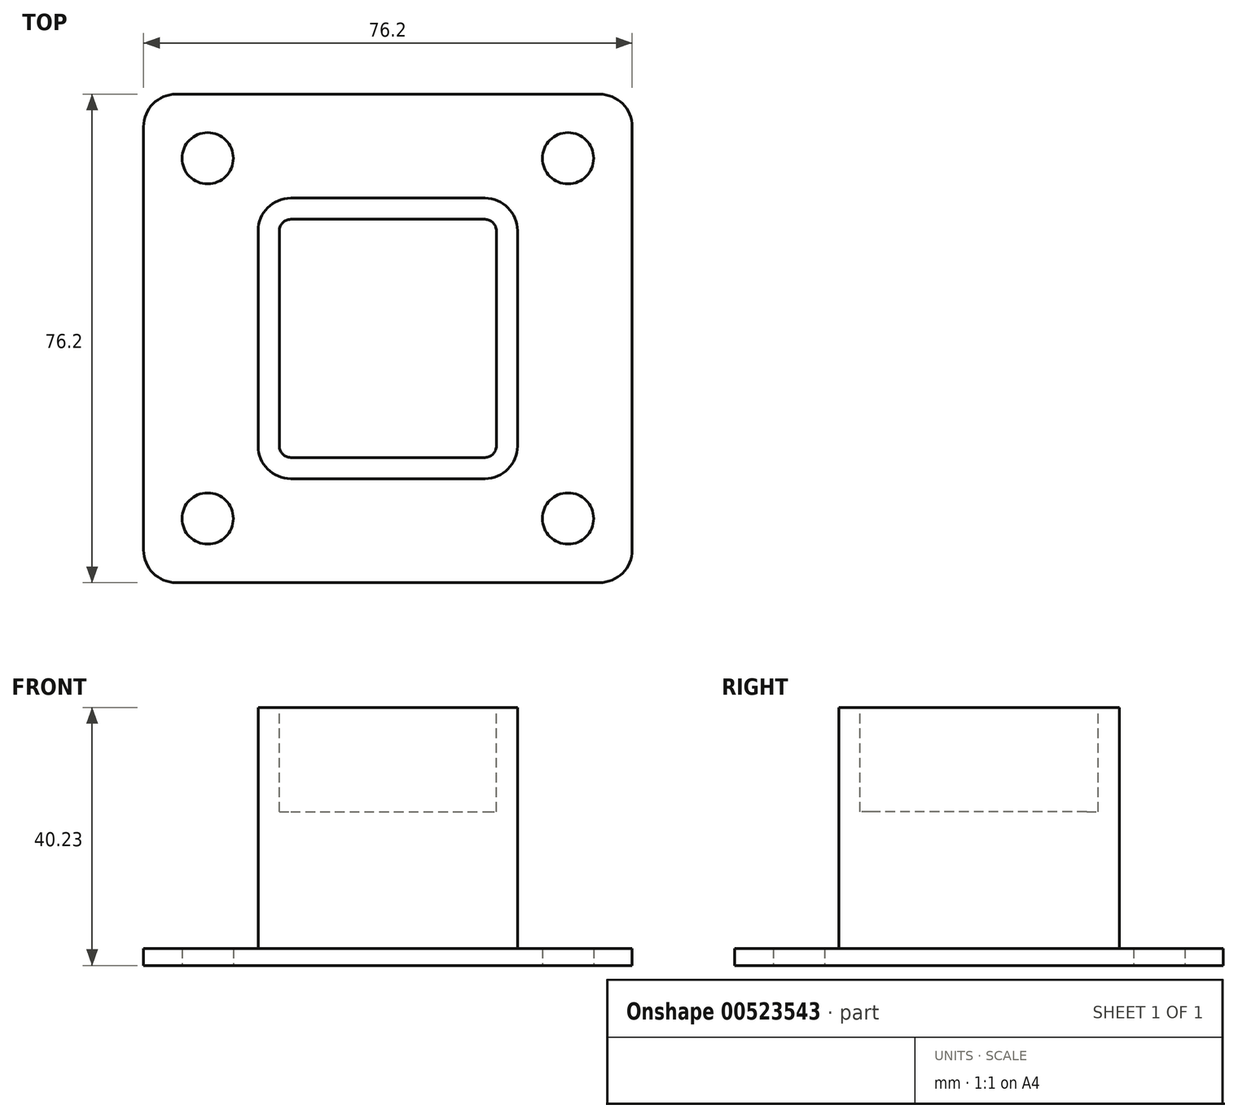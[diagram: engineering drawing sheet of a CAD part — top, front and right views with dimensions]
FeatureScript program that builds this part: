
annotation { "Feature Type Name" : "Feature", "Feature Type Description" : "" }
export const myFeature = defineFeature(function(context is Context, id is Id, definition is map)
    precondition{}
    {
        {
            var Q0;
            Q0=qCreatedBy(makeId("Top.planeOp"),FACE);
            var sketch = newSketch(context, id + "F0", { "sketchPlane" : qUnion([Q0])});
            skLineSegment(sketch, "E0.bottom", {"start": v(38.1, 38.1) * mm, "end": v(-38.1, 38.1) * mm});
            skLineSegment(sketch, "E0.top", {"start": v(38.1, -38.1) * mm, "end": v(-38.1, -38.1) * mm});
            skLineSegment(sketch, "E0.left", {"start": v(38.1, 38.1) * mm, "end": v(38.1, -38.1) * mm});
            skLineSegment(sketch, "E0.right", {"start": v(-38.1, 38.1) * mm, "end": v(-38.1, -38.1) * mm});
            skPoint(sketch, "E0.middle", {"position": v(0, 0) * mm});
            skLineSegment(sketch, "E1.bottom", {"start": v(28.1, 28.1) * mm, "end": v(-28.1, 28.1) * mm, "construction": true});
            skLineSegment(sketch, "E1.top", {"start": v(28.1, -28.1) * mm, "end": v(-28.1, -28.1) * mm, "construction": true});
            skLineSegment(sketch, "E1.left", {"start": v(28.1, 28.1) * mm, "end": v(28.1, -28.1) * mm, "construction": true});
            skLineSegment(sketch, "E1.right", {"start": v(-28.1, 28.1) * mm, "end": v(-28.1, -28.1) * mm, "construction": true});
            skCircle(sketch, "E2", {"center": v(-28.1, 28.1) * mm, "radius": 4 * mm});
            skCircle(sketch, "E3", {"center": v(28.1, 28.1) * mm, "radius": 4 * mm});
            skCircle(sketch, "E4", {"center": v(-28.1, -28.1) * mm, "radius": 4 * mm});
            skCircle(sketch, "E5", {"center": v(28.1, -28.1) * mm, "radius": 4 * mm});
            skSolve(sketch);
        }
        {
            var Q0;
            Q0 = qSketchRegion(id + "F0", true);
            extrude(context, id + "F1", {"entities" : qUnion([Q0]), "depth" : 2.64 * mm, "offsetDistance" : 25.4 * mm});
        }
        {
            var Q0;
            Q0=makeQuery(id+"F1.opExtrude","SWEPT_EDGE",EDGE,{"disambiguationData":[OSD([sQuery(id+"F0.wireOp",EDGE,"E0.top"),sQuery(id+"F0.wireOp",EDGE,"E0.right")])]});
            var Q1;
            Q1=makeQuery(id+"F1.opExtrude","SWEPT_EDGE",EDGE,{"disambiguationData":[OSD([sQuery(id+"F0.wireOp",EDGE,"E0.top"),sQuery(id+"F0.wireOp",EDGE,"E0.left")])]});
            var Q2;
            Q2=makeQuery(id+"F1.opExtrude","SWEPT_EDGE",EDGE,{"disambiguationData":[OSD([sQuery(id+"F0.wireOp",EDGE,"E0.bottom"),sQuery(id+"F0.wireOp",EDGE,"E0.left")])]});
            var Q3;
            Q3=makeQuery(id+"F1.opExtrude","SWEPT_EDGE",EDGE,{"disambiguationData":[OSD([sQuery(id+"F0.wireOp",EDGE,"E0.bottom"),sQuery(id+"F0.wireOp",EDGE,"E0.right")])]});
            fillet(context, id + "F2", {"entities" : qUnion([Q0, Q1, Q2, Q3]), "radius" : 5.08 * mm, "tangentPropagation" : true, "allowEdgeOverflow" : false});
        }
        {
            var Q0;
            Q0=makeQuery(id+"F1.opExtrude","CAP_FACE",FACE,{"disambiguationData":[OSD([sQuery(id+"F0.wireOp",EDGE,"E0.bottom"),sQuery(id+"F0.wireOp",EDGE,"E0.top"),sQuery(id+"F0.wireOp",EDGE,"E0.left"),sQuery(id+"F0.wireOp",EDGE,"E0.right"),sQuery(id+"F0.wireOp",EDGE,"E2"),sQuery(id+"F0.wireOp",EDGE,"E3"),sQuery(id+"F0.wireOp",EDGE,"E4"),sQuery(id+"F0.wireOp",EDGE,"E5")])],"isStart":false});
            var sketch = newSketch(context, id + "F3", { "sketchPlane" : qUnion([Q0])});
            skLineSegment(sketch, "E6.bottom", {"start": v(20.23, 21.88) * mm, "end": v(-20.23, 21.88) * mm});
            skLineSegment(sketch, "E6.top", {"start": v(20.23, -21.88) * mm, "end": v(-20.23, -21.88) * mm});
            skLineSegment(sketch, "E6.left", {"start": v(20.23, 21.88) * mm, "end": v(20.23, -21.88) * mm});
            skLineSegment(sketch, "E6.right", {"start": v(-20.23, 21.88) * mm, "end": v(-20.23, -21.88) * mm});
            skPoint(sketch, "E6.middle", {"position": v(0, 0) * mm});
            skSolve(sketch);
        }
        {
            var Q0;
            Q0 = qSketchRegion(id + "F3", true);
            extrude(context, id + "F4", {"entities" : qUnion([Q0]), "operationType" : NewBodyOperationType.ADD, "depth" : 37.6 * mm, "offsetDistance" : 25.4 * mm});
        }
        {
            var Q0;
            Q0=makeQuery(id+"F4.opExtrude","SWEPT_EDGE",EDGE,{"disambiguationData":[OSD([sQuery(id+"F3.wireOp",EDGE,"E6.top"),sQuery(id+"F3.wireOp",EDGE,"E6.right")])]});
            var Q1;
            Q1=makeQuery(id+"F4.opExtrude","SWEPT_EDGE",EDGE,{"disambiguationData":[OSD([sQuery(id+"F3.wireOp",EDGE,"E6.top"),sQuery(id+"F3.wireOp",EDGE,"E6.left")])]});
            var Q2;
            Q2=makeQuery(id+"F4.opExtrude","SWEPT_EDGE",EDGE,{"disambiguationData":[OSD([sQuery(id+"F3.wireOp",EDGE,"E6.bottom"),sQuery(id+"F3.wireOp",EDGE,"E6.left")])]});
            var Q3;
            Q3=makeQuery(id+"F4.opExtrude","SWEPT_EDGE",EDGE,{"disambiguationData":[OSD([sQuery(id+"F3.wireOp",EDGE,"E6.bottom"),sQuery(id+"F3.wireOp",EDGE,"E6.right")])]});
            fillet(context, id + "F5", {"entities" : qUnion([Q0, Q1, Q2, Q3]), "radius" : 5.08 * mm, "tangentPropagation" : true, "allowEdgeOverflow" : false});
        }
        {
            var Q0;
            Q0=makeQuery(id+"F4.opExtrude","CAP_FACE",FACE,{"disambiguationData":[OSD([sQuery(id+"F3.wireOp",EDGE,"E6.bottom"),sQuery(id+"F3.wireOp",EDGE,"E6.top"),sQuery(id+"F3.wireOp",EDGE,"E6.left"),sQuery(id+"F3.wireOp",EDGE,"E6.right")])],"isStart":false});
            var sketch = newSketch(context, id + "F6", { "sketchPlane" : qUnion([Q0])});
            skArc(sketch, "E7.0", {"start": v(-16.92, -16.8) * mm, "mid": v(-16.4, -18.06) * mm, "end": v(-15.15, -18.58) * mm});
            skLineSegment(sketch, "E7.1", {"start": v(-16.92, 16.8) * mm, "end": v(-16.92, -16.8) * mm});
            skLineSegment(sketch, "E7.2", {"start": v(-15.15, -18.58) * mm, "end": v(15.15, -18.58) * mm});
            skArc(sketch, "E7.3", {"start": v(-15.15, 18.58) * mm, "mid": v(-16.4, 18.06) * mm, "end": v(-16.92, 16.8) * mm});
            skArc(sketch, "E7.4", {"start": v(15.15, -18.58) * mm, "mid": v(16.4, -18.06) * mm, "end": v(16.92, -16.8) * mm});
            skLineSegment(sketch, "E7.5", {"start": v(16.92, -16.8) * mm, "end": v(16.92, 16.8) * mm});
            skArc(sketch, "E7.6", {"start": v(16.92, 16.8) * mm, "mid": v(16.4, 18.06) * mm, "end": v(15.15, 18.58) * mm});
            skLineSegment(sketch, "E7.7", {"start": v(15.15, 18.58) * mm, "end": v(-15.15, 18.58) * mm});
            skSolve(sketch);
        }
        {
            var Q0;
            Q0=makeQuery(id+"F6.imprint","IMPRINT",FACE,{"disambiguationData":[TD([[makeQuery(id+"F6.imprint","IMPRINT",EDGE,{"derivedFrom":sQuery(id+"F6.wireOp",EDGE,"E7.0")}),1.0]])]});
            extrude(context, id + "F7", {"entities" : qUnion([Q0]), "operationType" : NewBodyOperationType.REMOVE, "oppositeDirection" : true, "depth" : 16.26 * mm, "offsetDistance" : 25.4 * mm});
        }
    });
